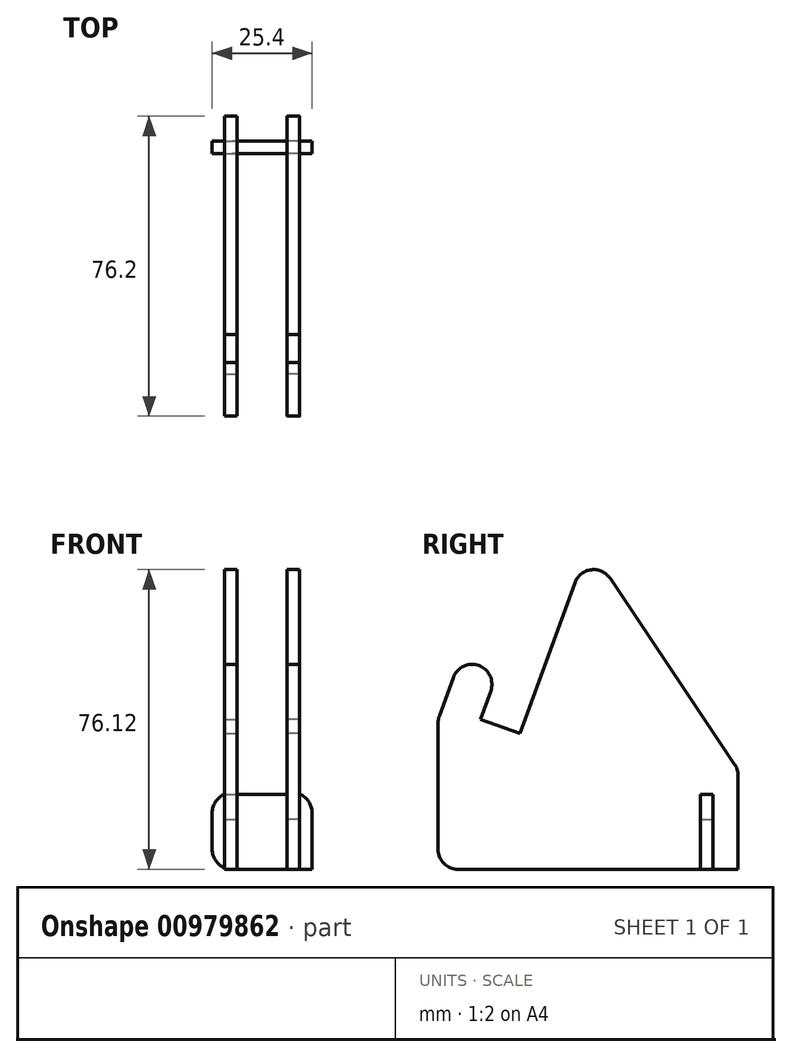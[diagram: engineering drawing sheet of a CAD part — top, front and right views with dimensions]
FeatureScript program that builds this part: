
annotation { "Feature Type Name" : "Feature", "Feature Type Description" : "" }
export const myFeature = defineFeature(function(context is Context, id is Id, definition is map)
    precondition{}
    {
        {
            var Q0;
            Q0=qCreatedBy(makeId("Right.planeOp"),FACE);
            var sketch = newSketch(context, id + "F0", { "sketchPlane" : qUnion([Q0])});
            skLineSegment(sketch, "E0", {"start": v(0, 0) * mm, "end": v(-6.35, 0) * mm});
            skLineSegment(sketch, "E1", {"start": v(-76.2, 0) * mm, "end": v(-76.2, 38.1) * mm});
            skLineSegment(sketch, "E2", {"start": v(-76.2, 38.1) * mm, "end": v(-70.6, 53.5) * mm});
            skLineSegment(sketch, "E3", {"start": v(-70.6, 53.5) * mm, "end": v(-61.1, 50.03) * mm});
            skLineSegment(sketch, "E4", {"start": v(-61.1, 50.03) * mm, "end": v(-65.43, 38.1) * mm});
            skLineSegment(sketch, "E5", {"start": v(-65.43, 38.1) * mm, "end": v(-55.41, 34.45) * mm});
            skLineSegment(sketch, "E6", {"start": v(-55.41, 34.45) * mm, "end": v(-38.04, 82.19) * mm});
            skLineSegment(sketch, "E7.top", {"start": v(-6.35, 12.7) * mm, "end": v(-9.52, 12.7) * mm});
            skLineSegment(sketch, "E7.left", {"start": v(-6.35, 0) * mm, "end": v(-6.35, 12.7) * mm});
            skLineSegment(sketch, "E7.right", {"start": v(-9.52, 0) * mm, "end": v(-9.53, 12.7) * mm});
            skPoint(sketch, "E8.start.orphan", {"position": v(-26.1, 38.1) * mm});
            skPoint(sketch, "E9.start.orphan", {"position": v(0, 50.8) * mm});
            skLineSegment(sketch, "E10", {"start": v(0, 0) * mm, "end": v(0, 25.4) * mm});
            skLineSegment(sketch, "E11", {"start": v(-38.04, 82.19) * mm, "end": v(0, 25.4) * mm});
            skLineSegment(sketch, "E12.trimOffspring", {"start": v(-9.52, 0) * mm, "end": v(-76.2, 0) * mm});
            skSolve(sketch);
        }
        {
            var Q0;
            Q0 = qSketchRegion(id + "F0", true);
            extrude(context, id + "F1", {"entities" : qUnion([Q0]), "depth" : 3.17 * mm, "offsetDistance" : 25.4 * mm});
        }
        {
            var Q0;
            Q0=makeQuery(id+"F1.opExtrude","SWEPT_FACE",FACE,{"disambiguationData":[OSD([sQuery(id+"F0.wireOp",EDGE,"E7.left")])]});
            var sketch = newSketch(context, id + "F2", { "sketchPlane" : qUnion([Q0])});
            skLineSegment(sketch, "E13.0.0", {"start": v(0, 12.7) * mm, "end": v(0, 0) * mm, "construction": true});
            skLineSegment(sketch, "E13.0.1", {"start": v(0, 0) * mm, "end": v(3.18, 0) * mm, "construction": true});
            skLineSegment(sketch, "E13.0.2", {"start": v(3.18, 0) * mm, "end": v(3.18, 12.7) * mm, "construction": true});
            skLineSegment(sketch, "E13.0.3", {"start": v(3.18, 12.7) * mm, "end": v(0, 12.7) * mm, "construction": true});
            skLineSegment(sketch, "E14", {"start": v(3.18, 12.7) * mm, "end": v(3.18, 19.05) * mm});
            skLineSegment(sketch, "E15", {"start": v(3.17, 19.05) * mm, "end": v(6.35, 19.05) * mm});
            skLineSegment(sketch, "E16", {"start": v(6.35, 19.05) * mm, "end": v(6.35, 0) * mm});
            skLineSegment(sketch, "E17", {"start": v(6.35, 0) * mm, "end": v(-19.05, 0) * mm});
            skLineSegment(sketch, "E18", {"start": v(-19.05, 0) * mm, "end": v(-19.05, 19.05) * mm});
            skLineSegment(sketch, "E19", {"start": v(-19.05, 19.05) * mm, "end": v(-15.87, 19.05) * mm});
            skLineSegment(sketch, "E20", {"start": v(-15.87, 19.05) * mm, "end": v(-15.87, 12.7) * mm});
            skLineSegment(sketch, "E21", {"start": v(-15.87, 12.7) * mm, "end": v(-12.7, 12.7) * mm});
            skLineSegment(sketch, "E22", {"start": v(-12.7, 12.7) * mm, "end": v(-12.7, 19.05) * mm});
            skLineSegment(sketch, "E23", {"start": v(-12.7, 19.05) * mm, "end": v(0, 19.05) * mm});
            skLineSegment(sketch, "E24", {"start": v(0, 19.05) * mm, "end": v(0, 12.7) * mm});
            skLineSegment(sketch, "E25", {"start": v(0, 12.7) * mm, "end": v(3.18, 12.7) * mm});
            skSolve(sketch);
        }
        {
            var Q0;
            Q0 = qSketchRegion(id + "F2", true);
            extrude(context, id + "F3", {"entities" : qUnion([Q0]), "depth" : 3.17 * mm, "offsetDistance" : 25.4 * mm});
        }
        {
            var Q0;
            Q0=makeQuery(id+"F1.opExtrude","SWEPT_EDGE",EDGE,{"disambiguationData":[OSD([sQuery(id+"F0.wireOp",EDGE,"E1"),sQuery(id+"F0.wireOp",EDGE,"E2")])]});
            var Q1;
            Q1=makeQuery(id+"F1.opExtrude","SWEPT_EDGE",EDGE,{"disambiguationData":[OSD([sQuery(id+"F0.wireOp",EDGE,"E2"),sQuery(id+"F0.wireOp",EDGE,"E3")])]});
            var Q2;
            Q2=makeQuery(id+"F1.opExtrude","SWEPT_EDGE",EDGE,{"disambiguationData":[OSD([sQuery(id+"F0.wireOp",EDGE,"E3"),sQuery(id+"F0.wireOp",EDGE,"E4")])]});
            var Q3;
            Q3=makeQuery(id+"F1.opExtrude","SWEPT_EDGE",EDGE,{"disambiguationData":[OSD([sQuery(id+"F0.wireOp",EDGE,"E6"),sQuery(id+"F0.wireOp",EDGE,"E11")])]});
            var Q4;
            Q4=makeQuery(id+"F1.opExtrude","SWEPT_EDGE",EDGE,{"disambiguationData":[OSD([sQuery(id+"F0.wireOp",EDGE,"E1"),sQuery(id+"F0.wireOp",EDGE,"E12.trimOffspring")])]});
            var Q5;
            Q5=makeQuery(id+"F1.opExtrude","SWEPT_EDGE",EDGE,{"disambiguationData":[OSD([sQuery(id+"F0.wireOp",EDGE,"E10"),sQuery(id+"F0.wireOp",EDGE,"E11")])]});
            var Q6;
            Q6=makeQuery(id+"F3.opExtrude","SWEPT_EDGE",EDGE,{"disambiguationData":[OSD([sQuery(id+"F2.wireOp",EDGE,"E15"),sQuery(id+"F2.wireOp",EDGE,"E16")])]});
            var Q7;
            Q7=makeQuery(id+"F3.opExtrude","SWEPT_EDGE",EDGE,{"disambiguationData":[OSD([sQuery(id+"F2.wireOp",EDGE,"E18"),sQuery(id+"F2.wireOp",EDGE,"E19")])]});
            var Q8;
            Q8=makeQuery(id+"F3.opExtrude","SWEPT_EDGE",EDGE,{"disambiguationData":[OSD([sQuery(id+"F2.wireOp",EDGE,"E17"),sQuery(id+"F2.wireOp",EDGE,"E18")])]});
            fillet(context, id + "F4", {"entities" : qUnion([Q0, Q1, Q2, Q3, Q4, Q5, Q6, Q7, Q8]), "radius" : 5.08 * mm, "tangentPropagation" : true, "allowEdgeOverflow" : false});
        }
        {
            var Q0;
            Q0=makeQuery(id+"F3.opExtrude","SWEPT_FACE",FACE,{"disambiguationData":[OSD([sQuery(id+"F2.wireOp",EDGE,"E22")])]});
            var sketch = newSketch(context, id + "F5", { "sketchPlane" : qUnion([Q0])});
            skArc(sketch, "E26.0.0", {"start": v(72.33, 48.72) * mm, "mid": v(69.72, 51.58) * mm, "end": v(65.84, 51.76) * mm});
            skArc(sketch, "E26.0.1", {"start": v(65.84, 51.76) * mm, "mid": v(63, 49.13) * mm, "end": v(62.83, 45.26) * mm});
            skLineSegment(sketch, "E26.0.2", {"start": v(62.83, 45.26) * mm, "end": v(65.43, 38.1) * mm});
            skLineSegment(sketch, "E26.0.3", {"start": v(65.43, 38.1) * mm, "end": v(55.41, 34.45) * mm});
            skLineSegment(sketch, "E26.0.4", {"start": v(55.41, 34.45) * mm, "end": v(41.46, 72.78) * mm});
            skArc(sketch, "E26.0.5", {"start": v(41.46, 72.78) * mm, "mid": v(37.3, 76.09) * mm, "end": v(32.46, 73.87) * mm});
            skLineSegment(sketch, "E26.0.6", {"start": v(32.46, 73.87) * mm, "end": v(0.86, 26.68) * mm});
            skArc(sketch, "E26.0.7", {"start": v(0.86, 26.68) * mm, "mid": v(0.22, 25.33) * mm, "end": v(0, 23.86) * mm});
            skLineSegment(sketch, "E26.0.8", {"start": v(0, 23.86) * mm, "end": v(0, 0) * mm});
            skLineSegment(sketch, "E26.0.9", {"start": v(0, 0) * mm, "end": v(6.35, 0) * mm});
            skLineSegment(sketch, "E26.0.10", {"start": v(6.35, 0) * mm, "end": v(6.35, 12.7) * mm});
            skLineSegment(sketch, "E26.0.11", {"start": v(6.35, 12.7) * mm, "end": v(9.52, 12.7) * mm});
            skLineSegment(sketch, "E26.0.12", {"start": v(9.53, 12.7) * mm, "end": v(9.52, 0) * mm});
            skLineSegment(sketch, "E26.0.13", {"start": v(9.52, 0) * mm, "end": v(71.12, 0) * mm});
            skArc(sketch, "E26.0.14", {"start": v(71.12, 0) * mm, "mid": v(74.71, 1.49) * mm, "end": v(76.2, 5.08) * mm});
            skLineSegment(sketch, "E26.0.15", {"start": v(76.2, 5.08) * mm, "end": v(76.2, 37.2) * mm});
            skArc(sketch, "E26.0.16", {"start": v(76.2, 37.2) * mm, "mid": v(76.12, 38.09) * mm, "end": v(75.9, 38.94) * mm});
            skLineSegment(sketch, "E26.0.17", {"start": v(75.9, 38.94) * mm, "end": v(72.33, 48.72) * mm});
            skSolve(sketch);
        }
        {
            var Q0;
            Q0=makeQuery(id+"F5.imprint","IMPRINT",FACE,{"disambiguationData":[TD([[makeQuery(id+"F5.imprint","IMPRINT",EDGE,{"derivedFrom":sQuery(id+"F5.wireOp",EDGE,"E26.0.0")}),1.0]])]});
            extrude(context, id + "F6", {"entities" : qUnion([Q0]), "depth" : 3.17 * mm, "offsetDistance" : 25.4 * mm});
        }
    });
